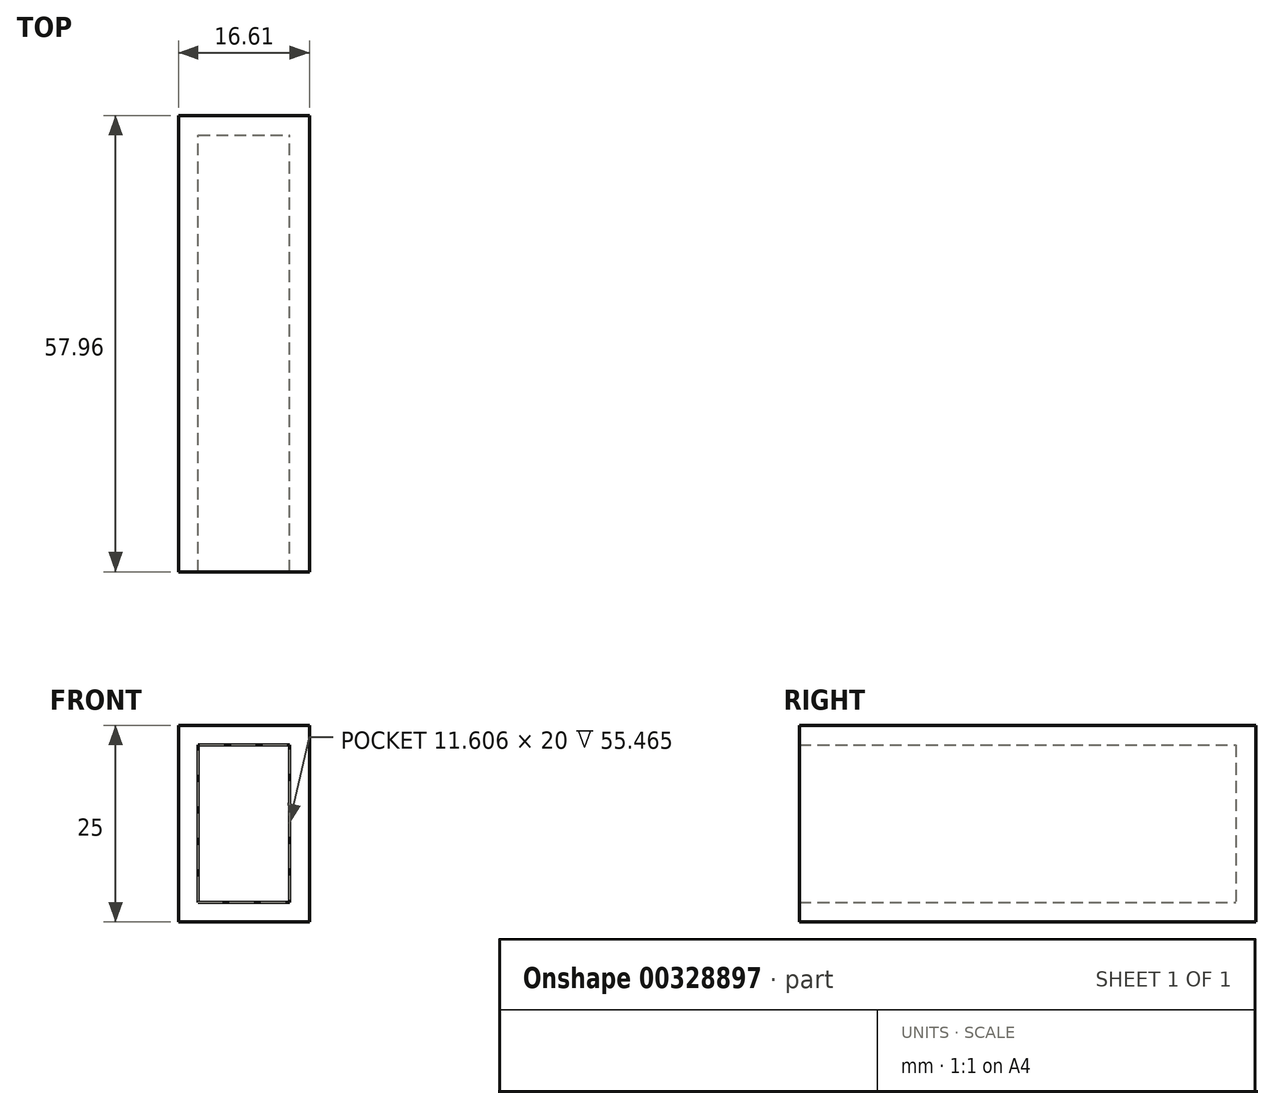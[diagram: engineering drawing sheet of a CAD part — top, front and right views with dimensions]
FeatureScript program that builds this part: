
annotation { "Feature Type Name" : "Feature", "Feature Type Description" : "" }
export const myFeature = defineFeature(function(context is Context, id is Id, definition is map)
    precondition{}
    {
        {
            var Q0;
            Q0=qCreatedBy(makeId("Top.planeOp"),FACE);
            var sketch = newSketch(context, id + "F0", { "sketchPlane" : qUnion([Q0])});
            skLineSegment(sketch, "E0.bottom", {"start": v(-16.6, 0) * mm, "end": v(0, 0) * mm});
            skLineSegment(sketch, "E0.top", {"start": v(-16.6, 57.96) * mm, "end": v(0, 57.96) * mm});
            skLineSegment(sketch, "E0.left", {"start": v(-16.6, 0) * mm, "end": v(-16.6, 57.96) * mm});
            skLineSegment(sketch, "E0.right", {"start": v(0, 0) * mm, "end": v(0, 57.96) * mm});
            skSolve(sketch);
        }
        {
            var Q0;
            Q0 = qSketchRegion(id + "F0", true);
            var sketch = newSketch(context, id + "F1", { "sketchPlane" : qUnion([Q0])});
            skSolve(sketch);
        }
        {
            var Q0;
            Q0=makeQuery(id+"F1.imprint","IMPRINT",FACE,{"disambiguationData":[TD([[makeQuery(id+"F1.imprint","IMPRINT",EDGE,{"derivedFrom":makeQuery(id+"F0.imprint","IMPRINT",EDGE,{"derivedFrom":sQuery(id+"F0.wireOp",EDGE,"E0.bottom")})}),1.0]])]});
            extrude(context, id + "F2", {"entities" : qUnion([Q0]), "depth" : 25 * mm});
        }
        {
            var Q0;
            Q0=makeQuery(id+"F2.opExtrude","SWEPT_FACE",FACE,{"disambiguationData":[OSD([sQuery(id+"F0.wireOp",EDGE,"E0.bottom")])]});
            shell(context, id + "F3", {"entities" : qUnion([Q0]), "thickness" : 2.5 * mm});
        }
    });
